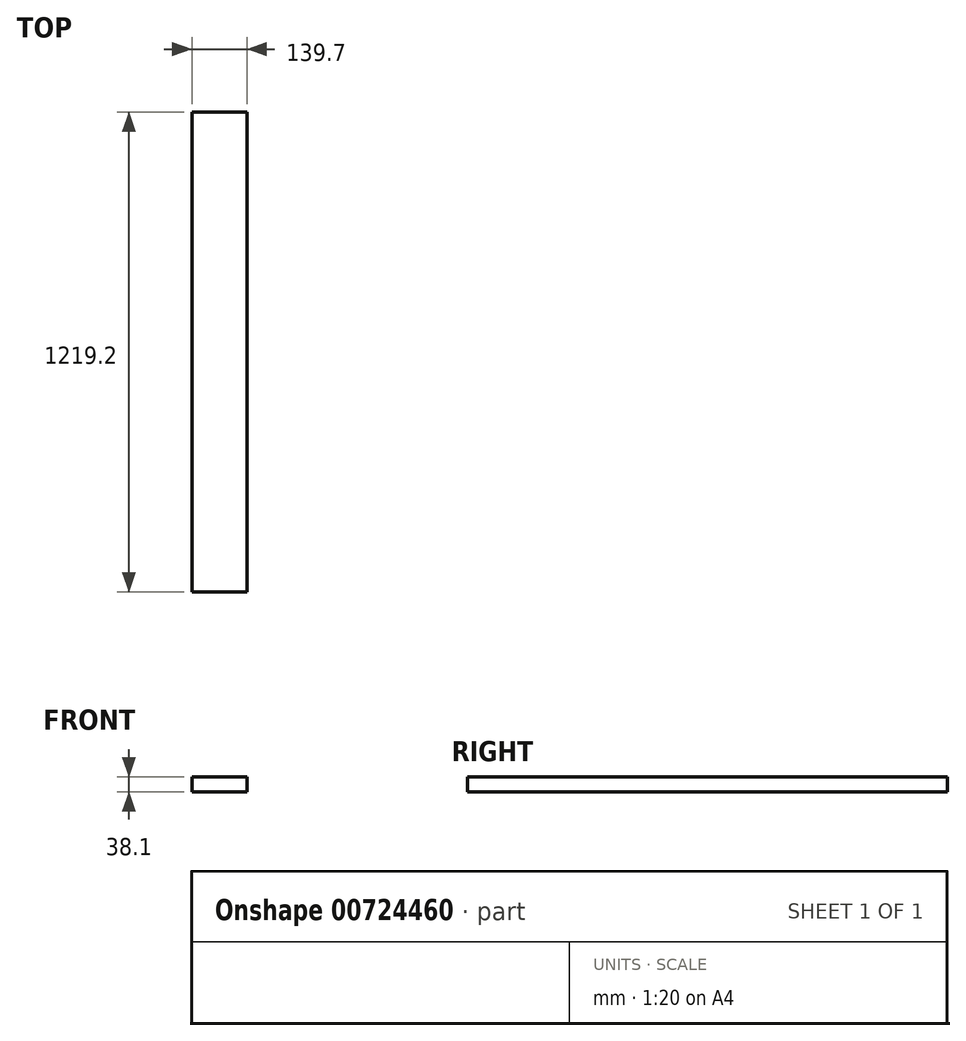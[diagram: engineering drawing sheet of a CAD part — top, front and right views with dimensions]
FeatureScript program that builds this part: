
annotation { "Feature Type Name" : "Feature", "Feature Type Description" : "" }
export const myFeature = defineFeature(function(context is Context, id is Id, definition is map)
    precondition{}
    {
        {
            var Q0;
            Q0=qCreatedBy(makeId("Front.planeOp"),FACE);
            var sketch = newSketch(context, id + "F0", { "sketchPlane" : qUnion([Q0])});
            skLineSegment(sketch, "E0.bottom", {"start": v(0, 0) * mm, "end": v(139.7, 0) * mm});
            skLineSegment(sketch, "E0.top", {"start": v(0, 38.1) * mm, "end": v(139.7, 38.1) * mm});
            skLineSegment(sketch, "E0.left", {"start": v(0, 0) * mm, "end": v(0, 38.1) * mm});
            skLineSegment(sketch, "E0.right", {"start": v(139.7, 0) * mm, "end": v(139.7, 38.1) * mm});
            skSolve(sketch);
        }
        {
            var Q0;
            Q0 = qSketchRegion(id + "F0", true);
            extrude(context, id + "F1", {"entities" : qUnion([Q0]), "oppositeDirection" : true, "depth" : 1219.2 * mm, "offsetDistance" : 25.4 * mm});
        }
    });
